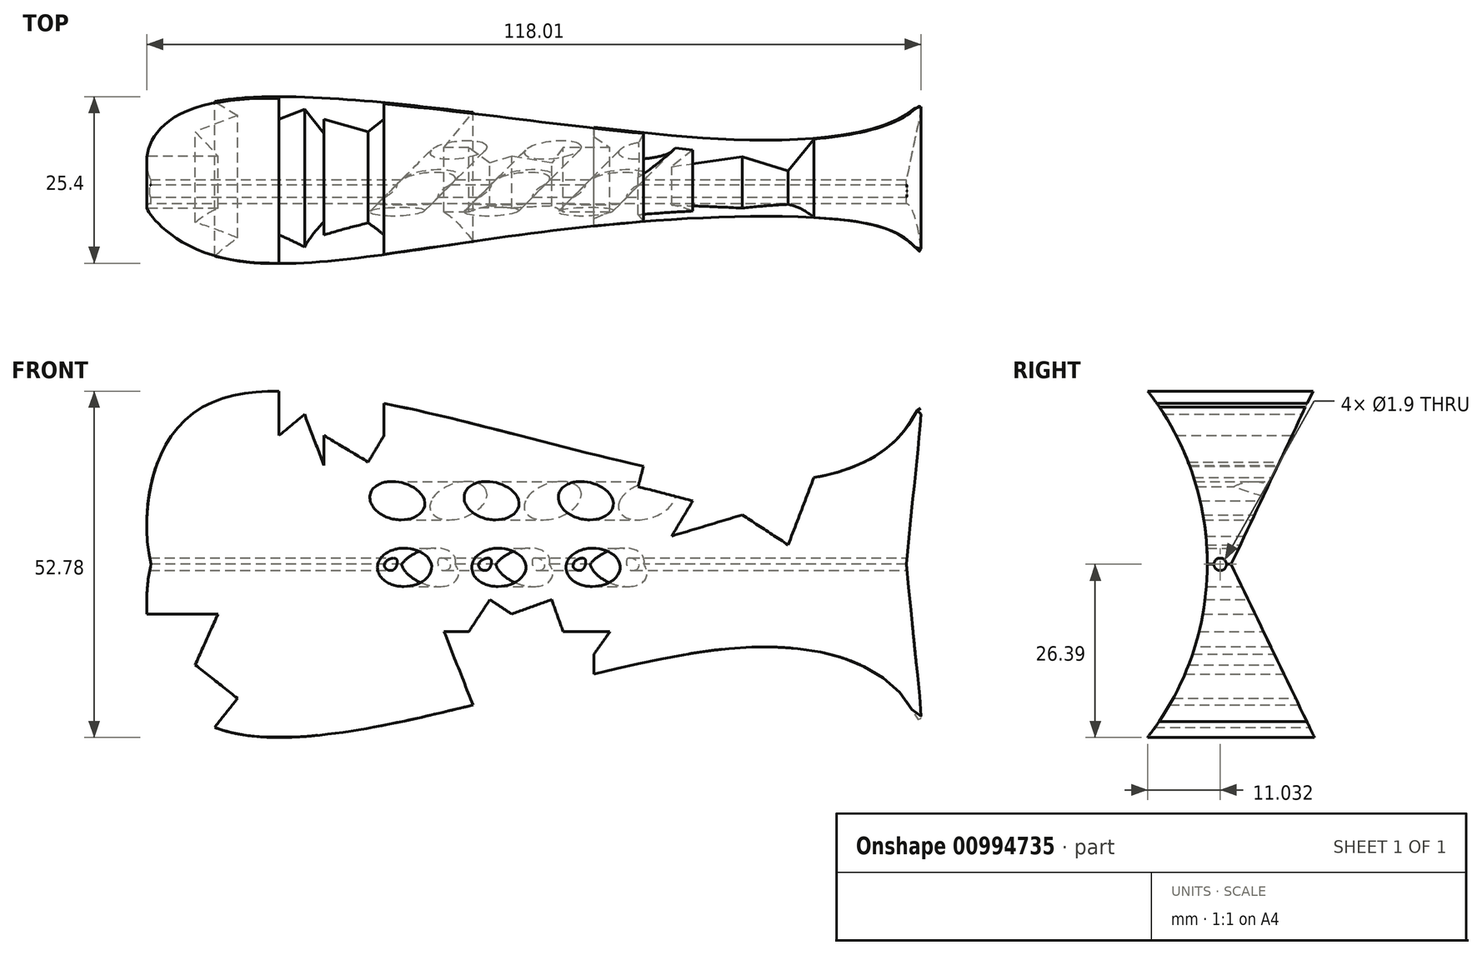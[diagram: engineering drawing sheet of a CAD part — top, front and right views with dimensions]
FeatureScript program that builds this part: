
annotation { "Feature Type Name" : "Feature", "Feature Type Description" : "" }
export const myFeature = defineFeature(function(context is Context, id is Id, definition is map)
    precondition{}
    {
        {
            var Q0;
            Q0=qCreatedBy(makeId("Front.planeOp"),FACE);
            var sketch = newSketch(context, id + "F0", { "sketchPlane" : qUnion([Q0])});
            skLineSegment(sketch, "E0", {"start": v(-64.68, 0) * mm, "end": v(62.53, 0) * mm, "construction": true});
            skFitSpline(sketch, "E1", {"points": [v(-64.68, 0) * mm, v(-56.38, 24.22) * mm, v(22.73, 12.9) * mm, v(50.16, 20.44) * mm, v(50.43, 0) * mm], "startDerivative": vector(-24.4, 98.96) * mm, "endDerivative": vector(-46.18, -481.54) * mm});
            skLineSegment(sketch, "E2", {"start": v(-64.68, 0) * mm, "end": v(50.43, 0) * mm});
            skFitSpline(sketch, "E3.MirrorCS", {"points": [v(-64.68, 0) * mm, v(-56.38, -24.22) * mm, v(22.73, -12.9) * mm, v(50.16, -20.44) * mm, v(50.43, 0) * mm], "startDerivative": vector(-24.4, -98.96) * mm, "endDerivative": vector(-46.18, 481.54) * mm});
            skSolve(sketch);
        }
        {
            var Q0;
            Q0 = qSketchRegion(id + "F0", true);
            extrude(context, id + "F1", {"entities" : qUnion([Q0]), "endBound" : BoundingType.SYMMETRIC, "depth" : 25.4 * mm, "offsetDistance" : 25.4 * mm});
        }
        {
            var Q0;
            Q0=qCreatedBy(makeId("Right.planeOp"),FACE);
            var sketch = newSketch(context, id + "F2", { "sketchPlane" : qUnion([Q0])});
            skLineSegment(sketch, "E4.0.1", {"start": v(12.7, 0) * mm, "end": v(-12.7, 0) * mm});
            skFitSpline(sketch, "E4.0.2", {"points": [v(-12.7, 0) * mm, v(-12.7, 8.8) * mm, v(-12.7, 17.6) * mm, v(-12.7, 26.4) * mm]});
            skLineSegment(sketch, "E4.0.3", {"start": v(-12.7, 0) * mm, "end": v(12.7, 0) * mm});
            skFitSpline(sketch, "E5.0.0", {"points": [v(12.7, 0) * mm, v(12.7, -8.8) * mm, v(12.7, -17.6) * mm, v(12.7, -26.4) * mm]});
            skArc(sketch, "E6", {"start": v(-12.7, -26.33) * mm, "mid": v(-3.63, 0.03) * mm, "end": v(-12.7, 26.4) * mm});
            skLineSegment(sketch, "E7", {"start": v(-12.7, 26.4) * mm, "end": v(-12.7, -26.33) * mm});
            skSolve(sketch);
        }
        {
            var Q0;
            {var subQ0=sQuery(id+"F2.wireOp",EDGE,"E7");var subQ1=sQuery(id+"F2.wireOp",EDGE,"E4.0.2");Q0=qUnion([makeQuery(id+"F2.imprint","IMPRINT",FACE,{"disambiguationData":[TD([[makeQuery(id+"F2.imprint","IMPRINT",EDGE,{"derivedFrom":subQ1}),-1.0]])]}),makeQuery(id+"F2.imprint","IMPRINT",FACE,{"disambiguationData":[TD([[makeQuery(id+"F2.imprint","IMPRINT",EDGE,{"derivedFrom":subQ0}),1.0]])]})]);}
            extrude(context, id + "F3", {"entities" : qUnion([Q0]), "operationType" : NewBodyOperationType.REMOVE, "endBound" : BoundingType.SYMMETRIC, "depth" : 254 * mm, "offsetDistance" : 25.4 * mm});
        }
        {
            var Q0;
            Q0=qCreatedBy(makeId("Right.planeOp"),FACE);
            var sketch = newSketch(context, id + "F4", { "sketchPlane" : qUnion([Q0])});
            skLineSegment(sketch, "E8.0.0", {"start": v(12.7, 0) * mm, "end": v(-3.63, 0) * mm});
            skArc(sketch, "E8.0.1", {"start": v(-12.7, 26.4) * mm, "mid": v(-5.95, 13.96) * mm, "end": v(-3.63, 0) * mm});
            skArc(sketch, "E8.0.3", {"start": v(-12.7, 26.4) * mm, "mid": v(-5.95, 13.96) * mm, "end": v(-3.63, 0) * mm});
            skLineSegment(sketch, "E8.0.4", {"start": v(-3.63, 0) * mm, "end": v(12.7, 0) * mm});
            skArc(sketch, "E9.0.0", {"start": v(-3.63, 0) * mm, "mid": v(-5.96, -13.92) * mm, "end": v(-12.7, -26.33) * mm});
            skFitSpline(sketch, "E9.0.1", {"points": [v(-12.7, -26.33) * mm, v(-12.7, -26.35) * mm, v(-12.7, -26.37) * mm, v(-12.7, -26.4) * mm]});
            skArc(sketch, "E9.0.2", {"start": v(-3.63, 0) * mm, "mid": v(-5.96, -13.92) * mm, "end": v(-12.7, -26.33) * mm});
            skFitSpline(sketch, "E9.0.4", {"points": [v(12.7, 0) * mm, v(12.7, -8.8) * mm, v(12.7, -17.6) * mm, v(12.7, -26.4) * mm]});
            skLineSegment(sketch, "E10", {"start": v(12.7, -26.4) * mm, "end": v(0, 0) * mm});
            skLineSegment(sketch, "E11", {"start": v(0, 0) * mm, "end": v(12.7, 26.9) * mm});
            skLineSegment(sketch, "E12", {"start": v(12.7, 26.9) * mm, "end": v(12.7, -26.4) * mm});
            skSolve(sketch);
        }
        {
            var Q0;
            {var subQ1=sQuery(id+"F4.wireOp",EDGE,"E9.0.4");var subQ3=sQuery(id+"F4.wireOp",EDGE,"E11");Q0=qUnion([makeQuery(id+"F4.imprint","IMPRINT",FACE,{"disambiguationData":[TD([[makeQuery(id+"F4.imprint","IMPRINT",EDGE,{"derivedFrom":subQ1}),-1.0]])]}),makeQuery(id+"F4.imprint","IMPRINT",FACE,{"disambiguationData":[TD([[makeQuery(id+"F4.imprint","IMPRINT",EDGE,{"derivedFrom":subQ3}),-1.0]])]})]);}
            extrude(context, id + "F5", {"entities" : qUnion([Q0]), "operationType" : NewBodyOperationType.REMOVE, "endBound" : BoundingType.SYMMETRIC, "depth" : 254 * mm, "offsetDistance" : 25.4 * mm});
        }
        {
            var Q0;
            Q0=qCreatedBy(makeId("Front.planeOp"),FACE);
            var sketch = newSketch(context, id + "F6", { "sketchPlane" : qUnion([Q0])});
            skFitSpline(sketch, "E13.0", {"points": [v(-45.18, 26.4) * mm, v(-44.5, 26.4) * mm, v(-43.12, 26.36) * mm, v(-40.4, 26.2) * mm, v(-37.05, 25.85) * mm, v(-33.07, 25.25) * mm, v(-27.8, 24.28) * mm, v(-21.27, 22.84) * mm, v(-13.46, 20.9) * mm, v(-5.66, 18.87) * mm, v(2.15, 16.87) * mm, v(8.7, 15.31) * mm, v(14, 14.22) * mm, v(18, 13.5) * mm, v(22.03, 12.94) * mm, v(25.4, 12.67) * mm, v(28.11, 12.59) * mm, v(30.16, 12.6) * mm, v(32.19, 12.7) * mm, v(34.2, 12.88) * mm, v(36.2, 13.17) * mm, v(38.18, 13.56) * mm, v(40.14, 14.08) * mm, v(42.08, 14.73) * mm, v(43.93, 15.53) * mm, v(45.4, 16.32) * mm, v(46.52, 17.04) * mm, v(47.32, 17.62) * mm, v(48.08, 18.24) * mm, v(48.8, 18.89) * mm, v(49.46, 19.58) * mm, v(50.07, 20.31) * mm, v(50.53, 20.95) * mm, v(50.87, 21.46) * mm, v(51.12, 21.85) * mm, v(51.36, 22.24) * mm, v(51.55, 22.57) * mm, v(51.7, 22.83) * mm, v(51.82, 23.03) * mm, v(51.93, 23.22) * mm, v(52.03, 23.38) * mm, v(52.1, 23.5) * mm, v(52.17, 23.6) * mm, v(52.23, 23.7) * mm, v(52.29, 23.77) * mm, v(52.34, 23.83) * mm, v(52.38, 23.87) * mm, v(52.42, 23.91) * mm, v(52.46, 23.94) * mm, v(52.5, 23.95) * mm, v(52.55, 23.94) * mm, v(52.58, 23.9) * mm, v(52.6, 23.85) * mm, v(52.62, 23.78) * mm, v(52.64, 23.7) * mm, v(52.65, 23.59) * mm, v(52.65, 23.48) * mm, v(52.66, 23.34) * mm, v(52.66, 23.16) * mm, v(52.65, 22.95) * mm, v(52.64, 22.73) * mm, v(52.63, 22.44) * mm, v(52.6, 22.08) * mm, v(52.57, 21.65) * mm, v(52.54, 21.2) * mm, v(52.5, 20.76) * mm, v(52.44, 20.17) * mm, v(52.37, 19.42) * mm, v(52.28, 18.51) * mm, v(52.19, 17.6) * mm, v(52.1, 16.68) * mm, v(51.97, 15.44) * mm, v(51.8, 13.87) * mm, v(51.61, 11.96) * mm, v(51.41, 10.02) * mm, v(51.22, 8.05) * mm, v(51.02, 6.05) * mm, v(50.82, 4.04) * mm, v(50.62, 2.03) * mm, v(50.5, 0.68) * mm, v(50.43, 0) * mm]});
            skLineSegment(sketch, "E14", {"start": v(-45.18, 26.4) * mm, "end": v(-45.18, 19.63) * mm});
            skLineSegment(sketch, "E15", {"start": v(-45.18, 19.63) * mm, "end": v(-41.28, 22.86) * mm});
            skLineSegment(sketch, "E16", {"start": v(-41.28, 22.86) * mm, "end": v(-38.32, 15.06) * mm});
            skLineSegment(sketch, "E17", {"start": v(-38.32, 15.06) * mm, "end": v(-38.32, 19.63) * mm});
            skLineSegment(sketch, "E18", {"start": v(-38.32, 19.63) * mm, "end": v(-31.6, 15.6) * mm});
            skLineSegment(sketch, "E19", {"start": v(-31.6, 15.6) * mm, "end": v(-29.18, 19.63) * mm});
            skLineSegment(sketch, "E20", {"start": v(-29.18, 19.63) * mm, "end": v(-29.18, 24.52) * mm});
            skLineSegment(sketch, "E21", {"start": v(-29.18, 24.52) * mm, "end": v(-29.18, 34.16) * mm});
            skLineSegment(sketch, "E22", {"start": v(-29.18, 34.16) * mm, "end": v(-45.18, 34.16) * mm});
            skLineSegment(sketch, "E23", {"start": v(-45.18, 26.4) * mm, "end": v(-45.18, 34.16) * mm});
            skFitSpline(sketch, "E24.0", {"points": [v(-64.68, 0) * mm, v(-64.87, -0.77) * mm, v(-65.15, -2.33) * mm, v(-65.32, -4.28) * mm, v(-65.36, -5.85) * mm, v(-65.34, -7.42) * mm, v(-65.2, -9.35) * mm, v(-64.9, -11.23) * mm, v(-64.57, -12.7) * mm, v(-64.28, -13.8) * mm, v(-63.93, -14.88) * mm, v(-63.42, -16.26) * mm, v(-62.65, -17.9) * mm, v(-61.7, -19.45) * mm, v(-60.81, -20.61) * mm, v(-59.85, -21.7) * mm, v(-58.77, -22.69) * mm, v(-57.56, -23.55) * mm, v(-56.26, -24.32) * mm, v(-54.88, -24.93) * mm, v(-53.41, -25.4) * mm, v(-52.28, -25.7) * mm, v(-51.12, -25.93) * mm, v(-49.57, -26.17) * mm, v(-48.39, -26.28) * mm, v(-47.6, -26.33) * mm]});
            skFitSpline(sketch, "E25.0", {"points": [v(-42.58, -26.33) * mm, v(-41.25, -26.26) * mm, v(-38.6, -26.03) * mm, v(-33.37, -25.33) * mm, v(-26.92, -24.12) * mm, v(-19.25, -22.35) * mm, v(-11.61, -20.42) * mm, v(-3.97, -18.43) * mm, v(3.7, -16.49) * mm, v(10.13, -15) * mm, v(15.32, -13.97) * mm, v(19.25, -13.31) * mm, v(23.2, -12.82) * mm, v(27.17, -12.57) * mm, v(31.18, -12.6) * mm, v(34.46, -12.9) * mm, v(37.06, -13.32) * mm, v(38.67, -13.69) * mm, v(39.95, -14.04) * mm, v(41.23, -14.44) * mm, v(42.77, -15.01) * mm, v(44.26, -15.7) * mm, v(45.4, -16.34) * mm, v(46.52, -17.03) * mm, v(47.56, -17.79) * mm, v(48.51, -18.62) * mm, v(49.19, -19.29) * mm, v(49.81, -19.99) * mm, v(50.28, -20.6) * mm, v(50.63, -21.1) * mm, v(50.88, -21.47) * mm, v(51.12, -21.85) * mm, v(51.35, -22.23) * mm, v(51.58, -22.61) * mm, v(51.76, -22.93) * mm, v(51.91, -23.18) * mm, v(52.02, -23.37) * mm, v(52.12, -23.53) * mm, v(52.2, -23.65) * mm, v(52.26, -23.74) * mm, v(52.32, -23.81) * mm, v(52.37, -23.87) * mm, v(52.41, -23.9) * mm, v(52.45, -23.94) * mm, v(52.5, -23.95) * mm, v(52.54, -23.95) * mm, v(52.58, -23.91) * mm, v(52.6, -23.87) * mm, v(52.62, -23.81) * mm, v(52.63, -23.75) * mm, v(52.64, -23.66) * mm, v(52.65, -23.56) * mm, v(52.66, -23.42) * mm, v(52.66, -23.24) * mm, v(52.66, -23.03) * mm, v(52.65, -22.82) * mm, v(52.63, -22.54) * mm, v(52.61, -22.18) * mm, v(52.58, -21.75) * mm, v(52.54, -21.32) * mm, v(52.5, -20.74) * mm, v(52.43, -20) * mm, v(52.34, -19.12) * mm, v(52.25, -18.23) * mm, v(52.13, -17.01) * mm, v(51.97, -15.48) * mm, v(51.78, -13.62) * mm, v(51.59, -11.74) * mm, v(51.4, -9.84) * mm, v(51.14, -7.27) * mm, v(50.88, -4.65) * mm, v(50.62, -2) * mm, v(50.5, -0.67) * mm, v(50.43, 0) * mm]});
            skLineSegment(sketch, "E26", {"start": v(-65.31, -7.56) * mm, "end": v(-54.48, -7.56) * mm});
            skLineSegment(sketch, "E27", {"start": v(-54.48, -7.56) * mm, "end": v(-57.96, -15.33) * mm});
            skLineSegment(sketch, "E28", {"start": v(-57.96, -15.33) * mm, "end": v(-51.5, -20.44) * mm});
            skLineSegment(sketch, "E29", {"start": v(-51.5, -20.44) * mm, "end": v(-55, -24.85) * mm});
            skLineSegment(sketch, "E30", {"start": v(-55, -24.85) * mm, "end": v(-66.83, -26.33) * mm});
            skLineSegment(sketch, "E31", {"start": v(-66.83, -26.33) * mm, "end": v(-65.31, -7.56) * mm});
            skLineSegment(sketch, "E32", {"start": v(-15.62, -21.43) * mm, "end": v(-20.02, -10.28) * mm});
            skLineSegment(sketch, "E33", {"start": v(-20.02, -10.28) * mm, "end": v(-16.27, -10.28) * mm});
            skLineSegment(sketch, "E34", {"start": v(-16.27, -10.28) * mm, "end": v(-13.04, -5.38) * mm});
            skLineSegment(sketch, "E35", {"start": v(-13.04, -5.38) * mm, "end": v(-9.73, -7.56) * mm});
            skLineSegment(sketch, "E36", {"start": v(-9.73, -7.56) * mm, "end": v(-3.63, -5.38) * mm});
            skLineSegment(sketch, "E37", {"start": v(-3.63, -5.38) * mm, "end": v(-1.88, -10.28) * mm});
            skLineSegment(sketch, "E38", {"start": v(-1.88, -10.28) * mm, "end": v(5.24, -10.28) * mm});
            skLineSegment(sketch, "E39", {"start": v(5.24, -10.28) * mm, "end": v(2.82, -13.72) * mm});
            skLineSegment(sketch, "E40", {"start": v(2.82, -13.72) * mm, "end": v(2.82, -16.73) * mm});
            skLineSegment(sketch, "E41", {"start": v(2.82, -16.73) * mm, "end": v(2.82, -24.85) * mm});
            skLineSegment(sketch, "E42", {"start": v(2.82, -24.85) * mm, "end": v(-15.62, -21.43) * mm});
            skLineSegment(sketch, "E43", {"start": v(36.33, 13.2) * mm, "end": v(32.4, 2.96) * mm});
            skLineSegment(sketch, "E44", {"start": v(32.4, 2.96) * mm, "end": v(25.41, 7.53) * mm});
            skLineSegment(sketch, "E45", {"start": v(25.41, 7.53) * mm, "end": v(14.66, 4.3) * mm});
            skLineSegment(sketch, "E46", {"start": v(14.66, 4.3) * mm, "end": v(17.88, 9.68) * mm});
            skLineSegment(sketch, "E47", {"start": v(17.88, 9.68) * mm, "end": v(9.55, 11.83) * mm});
            skLineSegment(sketch, "E48", {"start": v(9.55, 11.83) * mm, "end": v(10.36, 14.98) * mm});
            skLineSegment(sketch, "E49", {"start": v(10.36, 14.98) * mm, "end": v(28.37, 21.52) * mm});
            skLineSegment(sketch, "E50", {"start": v(28.37, 21.52) * mm, "end": v(36.33, 13.2) * mm});
            skSolve(sketch);
        }
        {
            var Q0;
            Q0 = qSketchRegion(id + "F6", true);
            extrude(context, id + "F7", {"entities" : qUnion([Q0]), "operationType" : NewBodyOperationType.REMOVE, "endBound" : BoundingType.SYMMETRIC, "depth" : 76.2 * mm, "offsetDistance" : 25.4 * mm});
        }
        {
            var Q0;
            Q0=qCreatedBy(makeId("Right.planeOp"),FACE);
            var Q1;
            Q1=qCreatedBy(makeId("Front.planeOp"),FACE);
            cPlane(context, id + "F8", {"entities" : qUnion([Q0, Q1]), "cplaneType" : CPlaneType.MID_PLANE, "offset" : 25.4 * mm, "width" : 152.4 * mm, "height" : 152.4 * mm});
        }
        {
            var Q0;
            Q0=qCreatedBy(id+"F8.planeOp",FACE);
            var sketch = newSketch(context, id + "F9", { "sketchPlane" : qUnion([Q0])});
            skEllipticalArc(sketch, "E51.0.0", {});
            skFitSpline(sketch, "E51.0.1", {"points": [v(-11.8, 14.98) * mm, v(-9.63, 15.7) * mm, v(-5.4, 17.3) * mm, v(0.7, 19.86) * mm, v(6.64, 22.38) * mm, v(10.6, 23.87) * mm, v(12.63, 24.52) * mm]});
            skEllipticalArc(sketch, "E51.0.2", {});
            skEllipticalArc(sketch, "E51.0.3", {});
            skEllipticalArc(sketch, "E51.0.4", {});
            skEllipticalArc(sketch, "E51.0.5", {});
            skEllipticalArc(sketch, "E51.0.6", {});
            skEllipticalArc(sketch, "E51.0.7", {});
            skEllipticalArc(sketch, "E51.0.8", {});
            skFitSpline(sketch, "E51.0.9", {"points": [v(-44.64, 0) * mm, v(-46.7, 30.42) * mm, v(-47.02, 18.36) * mm, v(-24.57, 5.2) * mm, v(35.62, 41.94) * mm, v(37.98, 7) * mm, v(36.76, 0) * mm]});
            skFitSpline(sketch, "E51.0.10", {"points": [v(22.97, 26.4) * mm, v(23.57, 26.4) * mm, v(24.78, 26.35) * mm, v(26.36, 26.15) * mm, v(27.66, 25.88) * mm, v(28.67, 25.61) * mm, v(29.7, 25.27) * mm, v(30.71, 24.87) * mm, v(31.74, 24.38) * mm, v(32.6, 23.9) * mm, v(33.27, 23.47) * mm, v(33.94, 23.02) * mm, v(34.75, 22.4) * mm, v(35.68, 21.61) * mm, v(36.58, 20.75) * mm, v(37.44, 19.82) * mm, v(38.24, 18.86) * mm, v(38.98, 17.86) * mm, v(39.9, 16.48) * mm, v(40.92, 14.66) * mm, v(41.92, 12.32) * mm, v(42.68, 9.93) * mm, v(43.11, 7.9) * mm, v(43.34, 6.23) * mm, v(43.48, 4.56) * mm, v(43.49, 2.48) * mm, v(43.31, 0.82) * mm, v(43.17, 0) * mm]});
            skFitSpline(sketch, "E51.0.11", {"points": [v(43.17, 0) * mm, v(43.28, -0.62) * mm, v(43.43, -1.88) * mm, v(43.5, -3.77) * mm, v(43.4, -5.66) * mm, v(43.24, -6.93) * mm, v(43.14, -7.56) * mm]});
            skLineSegment(sketch, "E51.0.12", {"start": v(43.14, -7.56) * mm, "end": v(35.48, -7.56) * mm});
            skEllipticalArc(sketch, "E51.0.13", {});
            skEllipticalArc(sketch, "E51.0.14", {});
            skEllipticalArc(sketch, "E51.0.15", {});
            skFitSpline(sketch, "E51.0.16", {"points": [v(30.69, -24.85) * mm, v(30.17, -25.08) * mm, v(29.13, -25.47) * mm, v(27.6, -25.9) * mm, v(26.1, -26.18) * mm, v(25.15, -26.29) * mm, v(24.67, -26.33) * mm]});
            skLineSegment(sketch, "E51.0.17", {"start": v(24.67, -26.33) * mm, "end": v(21.13, -26.33) * mm});
            skFitSpline(sketch, "E51.0.18", {"points": [v(21.13, -26.33) * mm, v(20.34, -26.27) * mm, v(18.82, -26.08) * mm, v(15.9, -25.51) * mm, v(12.44, -24.52) * mm, v(8.41, -23.07) * mm, v(5.74, -21.99) * mm, v(4.4, -21.43) * mm]});
            skEllipticalArc(sketch, "E51.0.19", {});
            skLineSegment(sketch, "E51.0.20", {"start": v(10.7, -10.28) * mm, "end": v(8.05, -10.28) * mm});
            skEllipticalArc(sketch, "E51.0.21", {});
            skEllipticalArc(sketch, "E51.0.22", {});
            skEllipticalArc(sketch, "E51.0.23", {});
            skEllipticalArc(sketch, "E51.0.24", {});
            skLineSegment(sketch, "E51.0.25", {"start": v(-2.13, -10.28) * mm, "end": v(-7.16, -10.28) * mm});
            skEllipticalArc(sketch, "E51.0.26", {});
            skEllipticalArc(sketch, "E51.0.27", {});
            skFitSpline(sketch, "E51.0.28", {"points": [v(-6.98, -16.73) * mm, v(-8, -16.33) * mm, v(-10.08, -15.55) * mm, v(-13.26, -14.49) * mm, v(-16.53, -13.57) * mm, v(-19.9, -12.87) * mm, v(-22.8, -12.59) * mm, v(-25.18, -12.59) * mm, v(-26.98, -12.72) * mm, v(-28.8, -12.98) * mm, v(-30.64, -13.4) * mm, v(-32.2, -13.91) * mm, v(-33.46, -14.42) * mm, v(-34.71, -15) * mm, v(-35.97, -15.69) * mm, v(-37.22, -16.5) * mm, v(-38.16, -17.18) * mm, v(-39.08, -17.91) * mm, v(-39.99, -18.7) * mm, v(-40.87, -19.55) * mm, v(-41.6, -20.31) * mm, v(-42.17, -20.94) * mm, v(-42.59, -21.41) * mm, v(-43, -21.9) * mm, v(-43.34, -22.3) * mm, v(-43.62, -22.62) * mm, v(-43.82, -22.86) * mm, v(-44.03, -23.1) * mm, v(-44.2, -23.3) * mm, v(-44.35, -23.45) * mm, v(-44.45, -23.57) * mm, v(-44.56, -23.69) * mm, v(-44.66, -23.78) * mm, v(-44.73, -23.85) * mm, v(-44.78, -23.9) * mm, v(-44.82, -23.92) * mm, v(-44.86, -23.94) * mm, v(-44.89, -23.95) * mm, v(-44.91, -23.94) * mm, v(-44.92, -23.91) * mm, v(-44.91, -23.87) * mm, v(-44.9, -23.82) * mm, v(-44.88, -23.75) * mm, v(-44.85, -23.67) * mm, v(-44.8, -23.56) * mm, v(-44.75, -23.42) * mm, v(-44.69, -23.3) * mm, v(-44.6, -23.11) * mm, v(-44.5, -22.9) * mm, v(-44.37, -22.62) * mm, v(-44.24, -22.35) * mm, v(-44.07, -22) * mm, v(-43.85, -21.54) * mm, v(-43.6, -21) * mm, v(-43.35, -20.44) * mm, v(-43.1, -19.88) * mm, v(-42.78, -19.14) * mm, v(-42.39, -18.2) * mm, v(-41.93, -17.04) * mm, v(-41.5, -15.88) * mm, v(-41.1, -14.71) * mm, v(-40.73, -13.54) * mm, v(-40.26, -11.95) * mm, v(-39.73, -9.95) * mm, v(-39.2, -7.51) * mm, v(-38.76, -5.04) * mm, v(-38.43, -2.52) * mm, v(-38.28, -0.84) * mm, v(-38.22, 0) * mm]});
            skFitSpline(sketch, "E51.0.29", {"points": [v(-38.22, 0) * mm, v(-38.29, 0.97) * mm, v(-38.46, 2.9) * mm, v(-38.87, 5.79) * mm, v(-39.42, 8.65) * mm, v(-40.1, 11.45) * mm, v(-40.77, 13.73) * mm, v(-41.36, 15.53) * mm, v(-41.84, 16.86) * mm, v(-42.27, 17.96) * mm, v(-42.63, 18.83) * mm, v(-42.9, 19.48) * mm, v(-43.18, 20.12) * mm, v(-43.47, 20.76) * mm, v(-43.71, 21.3) * mm, v(-43.9, 21.71) * mm, v(-44.06, 22.02) * mm, v(-44.2, 22.34) * mm, v(-44.35, 22.65) * mm, v(-44.47, 22.9) * mm, v(-44.57, 23.1) * mm, v(-44.64, 23.26) * mm, v(-44.71, 23.42) * mm, v(-44.77, 23.54) * mm, v(-44.8, 23.64) * mm, v(-44.84, 23.72) * mm, v(-44.86, 23.8) * mm, v(-44.88, 23.86) * mm, v(-44.88, 23.9) * mm, v(-44.88, 23.94) * mm, v(-44.86, 23.95) * mm, v(-44.82, 23.94) * mm, v(-44.78, 23.92) * mm, v(-44.73, 23.88) * mm, v(-44.68, 23.83) * mm, v(-44.6, 23.77) * mm, v(-44.52, 23.68) * mm, v(-44.42, 23.57) * mm, v(-44.3, 23.43) * mm, v(-44.13, 23.25) * mm, v(-43.93, 23.01) * mm, v(-43.69, 22.73) * mm, v(-43.37, 22.36) * mm, v(-42.97, 21.9) * mm, v(-42.49, 21.33) * mm, v(-42, 20.78) * mm, v(-41.5, 20.24) * mm, v(-41, 19.71) * mm, v(-40.32, 19.04) * mm, v(-39.46, 18.25) * mm, v(-38.4, 17.38) * mm, v(-37.32, 16.58) * mm, v(-35.87, 15.63) * mm, v(-34.42, 14.86) * mm, v(-32.96, 14.22) * mm, v(-31.5, 13.68) * mm, v(-30.44, 13.37) * mm, v(-29.73, 13.2) * mm]});
            skEllipticalArc(sketch, "E51.0.30", {});
            skEllipticalArc(sketch, "E51.0.31", {});
            skEllipticalArc(sketch, "E51.0.32", {});
            skEllipticalArc(sketch, "E51.0.33", {});
            skEllipticalArc(sketch, "E51.0.34", {});
            skCircle(sketch, "E52", {"center": v(15.85, 9.7) * mm, "radius": 2.93 * mm});
            skCircle(sketch, "E53.0.1.0", {"center": v(15.85, -0.46) * mm, "radius": 2.93 * mm});
            skCircle(sketch, "E53.1.0.0", {"center": v(5.69, 9.7) * mm, "radius": 2.93 * mm});
            skCircle(sketch, "E53.1.1.0", {"center": v(5.69, -0.46) * mm, "radius": 2.93 * mm});
            skCircle(sketch, "E53.2.0.0", {"center": v(-4.47, 9.7) * mm, "radius": 2.93 * mm});
            skCircle(sketch, "E53.2.1.0", {"center": v(-4.47, -0.46) * mm, "radius": 2.93 * mm});
            skLineSegment(sketch, "E53.direction1", {"start": v(15.85, 9.7) * mm, "end": v(5.69, 9.7) * mm, "construction": true});
            skLineSegment(sketch, "E53.direction2", {"start": v(15.85, 9.7) * mm, "end": v(15.85, -0.46) * mm, "construction": true});
            const initialGuessF9  = {"E51.0.0": [-0.037448251193241765, 3.403124777955936e-05, 0.325776705779815, -0.945446739891387, 0.04415611857617649, 0.02937599574662618, 1.6245548818535938, 1.7018900433804904], "E51.0.2": [-0.012216894761693606, 3.403124777955936e-05, 0, -1, 0.04283011521751002, 0.030285464909302475, 2.046080338298828, 2.1794261229946374], "E51.0.3": [-0.003901882244113547, 3.403124777955936e-05, 0.5688299552390124, -0.8224551550223168, 0.04871031345630355, 0.02662947247598591, 1.5812238221436192, 1.684590677767372], "E51.0.4": [-0.028848373087094075, 3.403124777955936e-05, 0.8224551550223169, 0.5688299552390124, 0.0704288654911931, 0.018417589754352696, 5.445795796796323, 5.549162652420076], "E51.0.5": [-0.0057511096950941965, 3.403124777955936e-05, 0, -1, 0.04283011521751002, 0.030285464909302475, 1.929268217783433, 2.0460803382988284], "E51.0.6": [-0.009781458067921597, 3.403124777955936e-05, 0.43374183834027835, 0.9010371899501128, 0.04551115431464451, 0.028501363479235986, 5.363660833694121, 5.567262723843562], "E51.0.7": [0.015848957572152284, 3.403124777955936e-05, 0.7528606698178295, -0.6581799236086203, 0.060230661987074545, 0.021536040094655526, 1.6578436250895048, 1.7446333947235515], "E51.0.8": [-0.0009010326986093437, 3.403124777955936e-05, 0, 1, 0.04283011521751002, 0.030285464909302475, 5.187672991888621, 5.375355378965077], "E51.0.13": [0.003267960891368542, 3.403124777955936e-05, 0.4827309741472183, -0.8757686946899149, 0.04641654721943967, 0.027945420958369594, 0.8834855108824781, 1.0721416340017493], "E51.0.14": [0.021853959002881528, 3.403124777955936e-05, 0.763029642908862, 0.6463634921948906, 0.06138923585207477, 0.02112959924451386, 4.599931320850808, 4.73144029160895], "E51.0.15": [-0.007893726855363874, 3.403124777955936e-05, 0.6463634921948909, -0.7630296429088619, 0.0520029087169583, 0.024943411503023948, 0.5648840712451312, 0.686460512545508], "E51.0.19": [-0.015818158959639186, 3.403124777955936e-05, 0.4451155655577906, 0.8954731337668196, 0.04570150017463753, 0.028382655854284976, 4.4868525111403414, 4.768661937390471], "E51.0.21": [-0.02614816293756963, 3.403124777955936e-05, 0.5955009577634065, -0.8033545974866054, 0.0496764519470211, 0.02611156595613237, 0.9561071853684018, 1.0725389315401028], "E51.0.22": [-0.017816256491200746, 3.403124777955936e-05, 0.8033545974866053, 0.5955009577634063, 0.067015519518807, 0.019355665087655696, 4.9056962225794445, 4.957209355547849], "E51.0.23": [-0.040995089644103415, 3.403124777955936e-05, 0.9092356344386197, -0.41628182889360044, 0.09881136058961626, 0.01312733620649681, 1.1101466278737255, 1.16165976084213], "E51.0.24": [-0.02891548230135189, 3.403124777955936e-05, 0.41628182889360044, 0.9092356344386197, 0.04523950925780319, 0.028672502703100046, 4.7516567800741205, 4.868088526245821], "E51.0.26": [-0.041691900060582175, 3.403124777955936e-05, 0.6141845690808792, -0.7891624136405224, 0.05044915783990522, 0.02571162744871935, 0.866356920177371, 0.9500304073068899], "E51.0.27": [-0.034847139643293695, 3.403124777955936e-05, 0, -1, 0.04283011521751002, 0.030285464909302475, 1.168695316340502, 1.2439725834478594], "E51.0.30": [-0.0549724271773368, 3.403124777955936e-05, 0.4367734631182586, -0.8995715324062247, 0.04556081765624379, 0.028470295710408943, 1.344606266105986, 1.5888785575589692], "E51.0.31": [-0.05893215357093357, 3.403124777955936e-05, 0.804992975472079, 0.5932843411388918, 0.06728621936684785, 0.019277795121899536, 5.151538421062339, 5.259082578380062], "E51.0.32": [-0.0331524264079769, 3.403124777955936e-05, 0.9304241227810344, -0.3664845859611874, 0.11318797682443965, 0.011459962337635883, 1.419038000454186, 1.4951294171667437], "E51.0.33": [-0.04140342925296179, 3.403124777955936e-05, 0.5688299535738052, -0.8224551561740147, 0.04871031340050206, 0.02662947250649207, 1.3091459565909043, 1.436515099731575], "E51.0.34": [-0.0719321262183094, 3.403124777955936e-05, 0.9454467398913871, 0.3257767057798152, 0.12814684909460516, 0.010122214948286929, 5.164940989343834, 5.216834687772859]};
            skSetInitialGuess(sketch, initialGuessF9);
            skSolve(sketch);
        }
        {
            var Q0;
            Q0=makeQuery(id+"F9.imprint","IMPRINT",FACE,{"disambiguationData":[TD([[makeQuery(id+"F9.imprint","IMPRINT",EDGE,{"derivedFrom":sQuery(id+"F9.wireOp",EDGE,"E53.0.1.0")}),1.0]])]});
            var Q1;
            Q1=makeQuery(id+"F9.imprint","IMPRINT",FACE,{"disambiguationData":[TD([[makeQuery(id+"F9.imprint","IMPRINT",EDGE,{"derivedFrom":sQuery(id+"F9.wireOp",EDGE,"E52")}),1.0]])]});
            var Q2;
            Q2=makeQuery(id+"F9.imprint","IMPRINT",FACE,{"disambiguationData":[TD([[makeQuery(id+"F9.imprint","IMPRINT",EDGE,{"derivedFrom":sQuery(id+"F9.wireOp",EDGE,"E53.1.0.0")}),1.0]])]});
            var Q3;
            Q3=makeQuery(id+"F9.imprint","IMPRINT",FACE,{"disambiguationData":[TD([[makeQuery(id+"F9.imprint","IMPRINT",EDGE,{"derivedFrom":sQuery(id+"F9.wireOp",EDGE,"E53.1.1.0")}),1.0]])]});
            var Q4;
            Q4=makeQuery(id+"F9.imprint","IMPRINT",FACE,{"disambiguationData":[TD([[makeQuery(id+"F9.imprint","IMPRINT",EDGE,{"derivedFrom":sQuery(id+"F9.wireOp",EDGE,"E53.2.1.0")}),1.0]])]});
            var Q5;
            Q5=makeQuery(id+"F9.imprint","IMPRINT",FACE,{"disambiguationData":[TD([[makeQuery(id+"F9.imprint","IMPRINT",EDGE,{"derivedFrom":sQuery(id+"F9.wireOp",EDGE,"E53.2.0.0")}),1.0]])]});
            extrude(context, id + "F10", {"entities" : qUnion([Q0, Q1, Q2, Q3, Q4, Q5]), "operationType" : NewBodyOperationType.REMOVE, "endBound" : BoundingType.SYMMETRIC, "oppositeDirection" : true, "depth" : 254 * mm, "offsetDistance" : 25.4 * mm});
        }
        {
            var Q0;
            Q0=qCreatedBy(makeId("Right.planeOp"),FACE);
            var sketch = newSketch(context, id + "F11", { "sketchPlane" : qUnion([Q0])});
            skCircle(sketch, "E54", {"center": v(-1.67, 0) * mm, "radius": 0.95 * mm});
            skSolve(sketch);
        }
        {
            var Q0;
            Q0 = qSketchRegion(id + "F11", true);
            extrude(context, id + "F12", {"entities" : qUnion([Q0]), "operationType" : NewBodyOperationType.REMOVE, "endBound" : BoundingType.SYMMETRIC, "oppositeDirection" : true, "depth" : 508 * mm, "offsetDistance" : 25.4 * mm});
        }
    });
